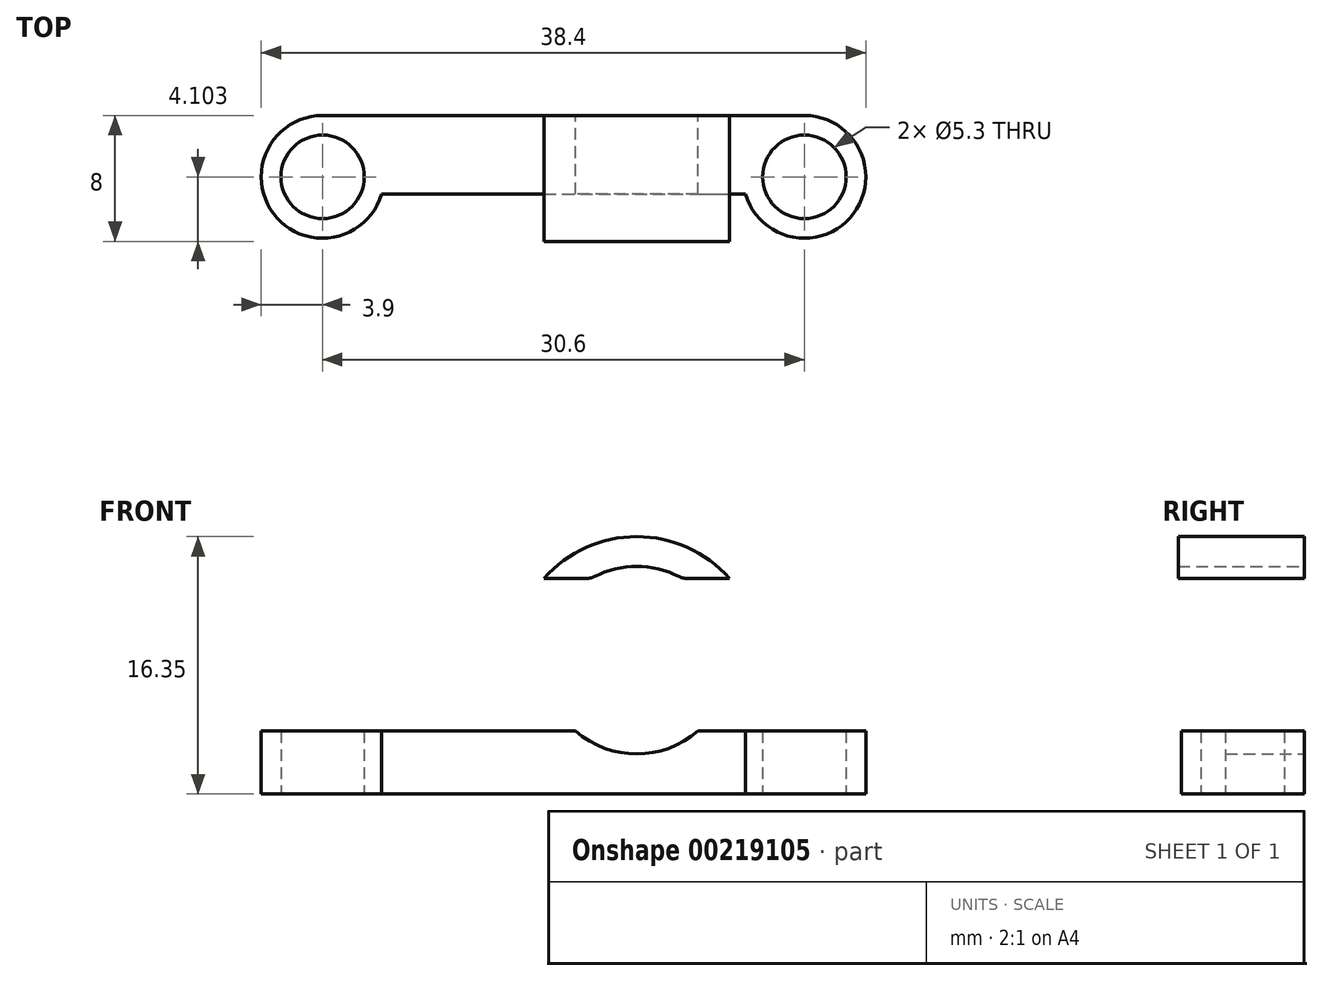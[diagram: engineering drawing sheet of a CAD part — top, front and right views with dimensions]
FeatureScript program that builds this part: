
annotation { "Feature Type Name" : "Feature", "Feature Type Description" : "" }
export const myFeature = defineFeature(function(context is Context, id is Id, definition is map)
    precondition{}
    {
        {
            var Q0;
            Q0=qCreatedBy(makeId("Top.planeOp"),FACE);
            var sketch = newSketch(context, id + "F0", { "sketchPlane" : qUnion([Q0])});
            skCircle(sketch, "E0", {"center": v(15.3, 9.57) * mm, "radius": 2.65 * mm});
            skCircle(sketch, "E1", {"center": v(15.3, 9.57) * mm, "radius": 3.9 * mm});
            skCircle(sketch, "E2", {"center": v(-15.3, 9.57) * mm, "radius": 3.9 * mm});
            skLineSegment(sketch, "E3", {"start": v(-15.3, 13.47) * mm, "end": v(15.3, 13.47) * mm});
            skLineSegment(sketch, "E4", {"start": v(-11.56, 8.47) * mm, "end": v(11.56, 8.47) * mm});
            skCircle(sketch, "E5", {"center": v(-15.3, 9.57) * mm, "radius": 2.65 * mm});
            skLineSegment(sketch, "E6", {"start": v(-2.5, 13.47) * mm, "end": v(-2.5, 8.47) * mm});
            skLineSegment(sketch, "E7", {"start": v(2.5, 13.47) * mm, "end": v(2.5, 8.47) * mm});
            skSolve(sketch);
        }
        {
            var Q0;
            Q0=makeQuery(id+"F0.imprint","IMPRINT",FACE,{"disambiguationData":[TD([[makeQuery(id+"F0.imprint","IMPRINT",EDGE,{"derivedFrom":sQuery(id+"F0.wireOp",EDGE,"E0")}),-1.0]])]});
            var Q1;
            Q1=makeQuery(id+"F0.imprint","IMPRINT",FACE,{"disambiguationData":[TD([[makeQuery(id+"F0.imprint","IMPRINT",EDGE,{"derivedFrom":sQuery(id+"F0.wireOp",EDGE,"E5")}),-1.0]])]});
            extrude(context, id + "F1", {"entities" : qUnion([Q0, Q1]), "depth" : 4 * mm});
        }
        {
            var Q0;
            {var subQ5=sQuery(id+"F0.wireOp",EDGE,"E6");Q0=makeQuery(id+"F0.imprint","IMPRINT",FACE,{"disambiguationData":[TD([[makeQuery(id+"F0.imprint","IMPRINT",EDGE,{"derivedFrom":subQ5}),-1.0]])]});}
            var Q1;
            {var subQ5=sQuery(id+"F0.wireOp",EDGE,"E7");Q1=makeQuery(id+"F0.imprint","IMPRINT",FACE,{"disambiguationData":[TD([[makeQuery(id+"F0.imprint","IMPRINT",EDGE,{"derivedFrom":subQ5}),1.0]])]});}
            extrude(context, id + "F2", {"entities" : qUnion([Q0, Q1]), "operationType" : NewBodyOperationType.ADD, "depth" : 4 * mm});
        }
        {
            var Q0;
            {var subQ0=sQuery(id+"F0.wireOp",EDGE,"E6");Q0=makeQuery(id+"F0.imprint","IMPRINT",FACE,{"disambiguationData":[TD([[makeQuery(id+"F0.imprint","IMPRINT",EDGE,{"derivedFrom":subQ0}),1.0]])]});}
            extrude(context, id + "F3", {"entities" : qUnion([Q0]), "operationType" : NewBodyOperationType.ADD, "depth" : 4 * mm});
        }
        {
            var Q0;
            {var subQ0=sQuery(id+"F0.wireOp",EDGE,"E3");Q0=makeQuery(id+"F3.boolean.opBoolean","MERGE",FACE,{"derivedFrom":[makeQuery(id+"F2.opExtrude","SWEPT_FACE",FACE,{"disambiguationData":[OSD([subQ0]),TDD([makeQuery(id+"F0.imprint","IMPRINT",EDGE,{"disambiguationData":[TD([[makeQuery(id+"F0.imprint","INTERSECT",VERTEX,{"derivedFrom":[sQuery(id+"F0.wireOp",EDGE,"E2"),subQ0]}),-1.0]])],"derivedFrom":subQ0})])]}),makeQuery(id+"F2.opExtrude","SWEPT_FACE",FACE,{"disambiguationData":[OSD([subQ0]),TDD([makeQuery(id+"F0.imprint","IMPRINT",EDGE,{"disambiguationData":[TD([[makeQuery(id+"F0.imprint","INTERSECT",VERTEX,{"derivedFrom":[sQuery(id+"F0.wireOp",EDGE,"E1"),subQ0]}),1.0]])],"derivedFrom":subQ0})])]}),makeQuery(id+"F3.opExtrude","SWEPT_FACE",FACE,{"disambiguationData":[OSD([subQ0])]})]});}
            cPlane(context, id + "F4", {"entities" : qUnion([Q0]), "cplaneType" : CPlaneType.OFFSET, "offset" : 0 * mm, "width" : 150 * mm, "height" : 150 * mm});
        }
        {
            var Q0;
            Q0=qCreatedBy(id+"F4.planeOp",FACE);
            var sketch = newSketch(context, id + "F5", { "sketchPlane" : qUnion([Q0])});
            skCircle(sketch, "E8", {"center": v(-4.65, 8.5) * mm, "radius": 5.95 * mm});
            skCircle(sketch, "E9.0", {"center": v(-4.65, 8.5) * mm, "radius": 7.85 * mm});
            skPoint(sketch, "E10.0", {"position": v(-11.56, 4) * mm});
            skLineSegment(sketch, "E11.0", {"start": v(-17.95, 0) * mm, "end": v(-12.65, 0) * mm});
            skLineSegment(sketch, "E12", {"start": v(-12.65, 0) * mm, "end": v(-12.65, 19.88) * mm});
            skLineSegment(sketch, "E13", {"start": v(-12.65, 13.7) * mm, "end": v(7.8, 13.7) * mm});
            skSolve(sketch);
        }
        {
            var Q0;
            {var subQ0=sQuery(id+"F5.wireOp",EDGE,"E13");var subQ1=sQuery(id+"F5.wireOp",EDGE,"E8");var subQ2=makeQuery(id+"F5.imprint","INTERSECT",VERTEX,{"disambiguationData":[OD(0.0)],"derivedFrom":[subQ1,subQ0]});Q0=makeQuery(id+"F5.imprint","IMPRINT",FACE,{"disambiguationData":[TD([[makeQuery(id+"F5.imprint","IMPRINT",EDGE,{"disambiguationData":[TD([[subQ2,-1.0]])],"derivedFrom":subQ1}),-1.0]])]});}
            extrude(context, id + "F6", {"entities" : qUnion([Q0]), "operationType" : NewBodyOperationType.ADD, "oppositeDirection" : true, "depth" : 8 * mm});
        }
        {
            var Q0;
            Q0=makeQuery(id+"F5.imprint","IMPRINT",FACE,{"disambiguationData":[TD([[makeQuery(id+"F5.imprint","IMPRINT",EDGE,{"derivedFrom":sQuery(id+"F5.wireOp",EDGE,"E8")}),1.0]])]});
            extrude(context, id + "F7", {"entities" : qUnion([Q0]), "operationType" : NewBodyOperationType.REMOVE, "oppositeDirection" : true, "depth" : 10 * mm});
        }
        {
            var Q0;
            {var subQ0=sQuery(id+"F5.wireOp",EDGE,"E13");var subQ1=sQuery(id+"F5.wireOp",EDGE,"E8");Q0=makeQuery(id+"F6.opExtrude","SWEPT_EDGE",EDGE,{"disambiguationData":[OSD([subQ1,subQ0]),TDD([makeQuery(id+"F5.imprint","INTERSECT",VERTEX,{"disambiguationData":[OD(0.0)],"derivedFrom":[subQ1,subQ0]})])]});}
            var Q1;
            {var subQ0=sQuery(id+"F5.wireOp",EDGE,"E13");var subQ1=sQuery(id+"F5.wireOp",EDGE,"E8");Q1=makeQuery(id+"F6.opExtrude","SWEPT_EDGE",EDGE,{"disambiguationData":[OSD([subQ1,subQ0]),TDD([makeQuery(id+"F5.imprint","INTERSECT",VERTEX,{"disambiguationData":[OD(1.0)],"derivedFrom":[subQ1,subQ0]})])]});}
            fillet(context, id + "F8", {"entities" : qUnion([Q0, Q1]), "radius" : 1 * mm, "tangentPropagation" : true, "allowEdgeOverflow" : false});
        }
    });
